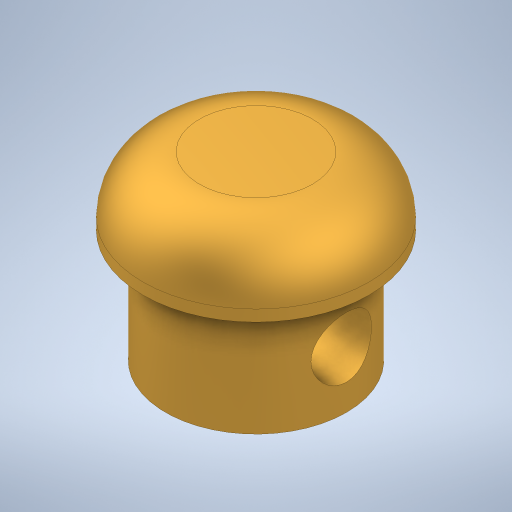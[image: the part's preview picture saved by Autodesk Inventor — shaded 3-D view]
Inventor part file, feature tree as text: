
AUTODESK INVENTOR PART (.ipt)
format: ipt  version: 2023 (Build 270158000, 158)  size: 280,576 bytes
history: native  units: in
note: dims shown in document units (in); Inventor stores cm internally (conversion verified against a paired STEP export)
features: sketch x3, extrude x2, fillet x1, plane x1, hole x1
ambient origin geometry x8: Origin, YZ Plane, XZ Plane, XY Plane, X Axis, Y Axis, Z Axis, Center Point
bodies: Solid1 (feature_tree)
feature tree (8):
  extrude  "Extrusion1"  Depth=0.25in TaperAngle=0.0deg
  extrude  "Extrusion2"  Depth=0.125in TaperAngle=0.0deg
  fillet  "Fillet1"  Radius=0.125in
  plane  "Work Plane1"
  hole  "Hole1"  [1 undecoded]
  sketch  "Sketch1"  dims[d0=0.4in d1=0.25in d2=0.0in]
  sketch  "Sketch2"  dims[d3=0.5in d4=0.15in d5=0.0in d6=0.125in]
  sketch  "Sketch3"  dims[d7=0.2in d8=0.125in d9=0.1339in d10=0.75in d11=0.256in d12=0.118in d13=90.0deg d14=1.0in d15=0.8108in]
note: 1 required parameter value undecoded (feature->parameter linkage not recoverable at this tier; creation-order binding heuristic only, values carry confidence <= 0.55)
